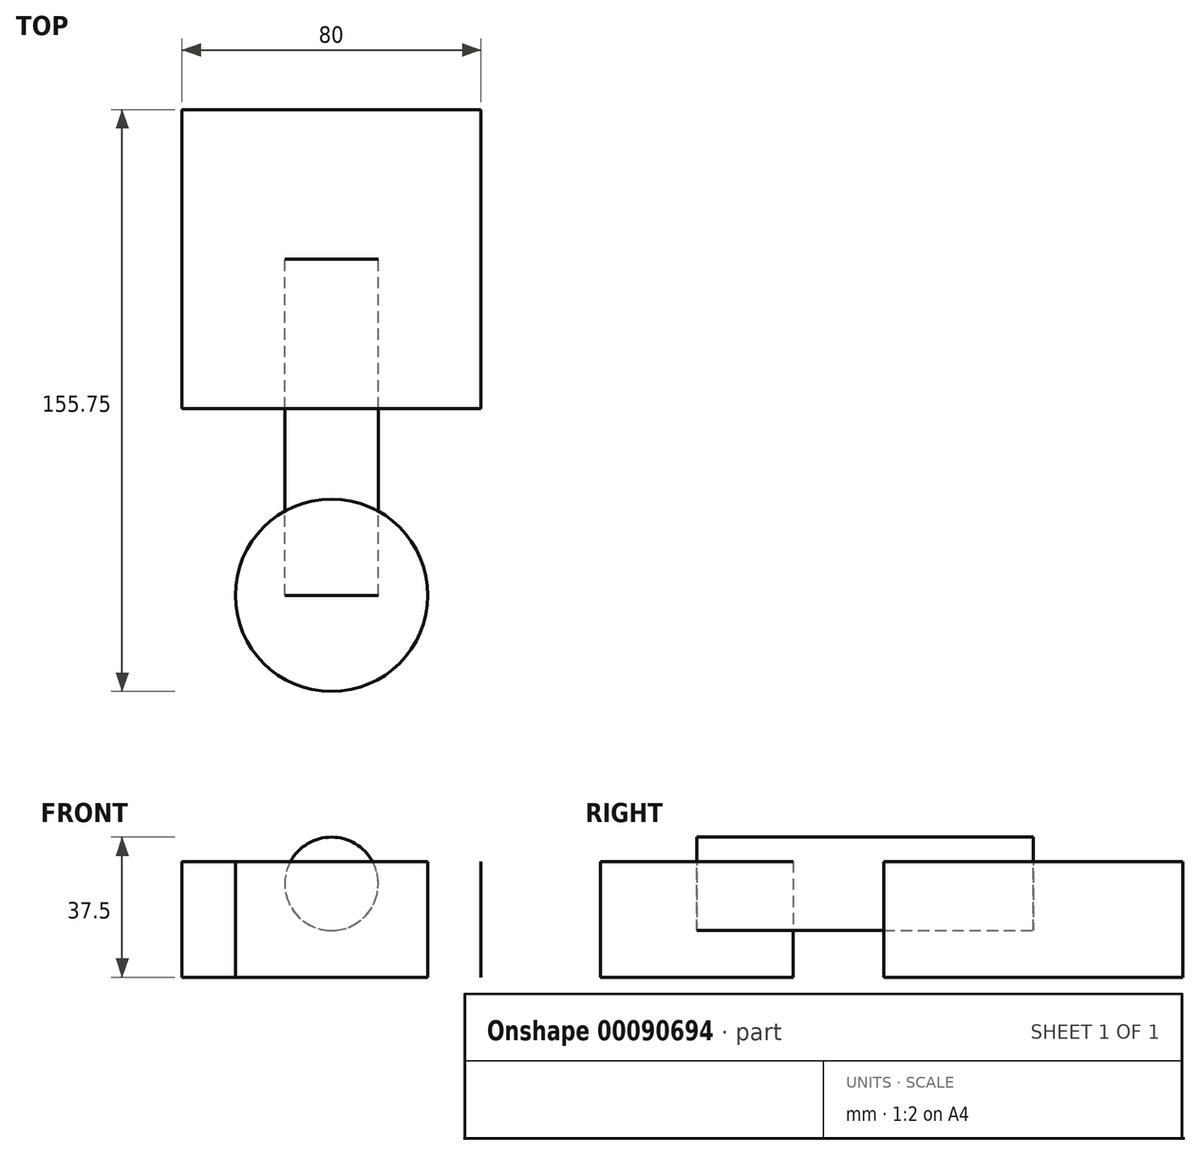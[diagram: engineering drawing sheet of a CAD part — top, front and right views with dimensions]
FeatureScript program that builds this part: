
annotation { "Feature Type Name" : "Feature", "Feature Type Description" : "" }
export const myFeature = defineFeature(function(context is Context, id is Id, definition is map)
    precondition{}
    {
        {
            var Q0;
            Q0=qCreatedBy(makeId("Top.planeOp"),FACE);
            var sketch = newSketch(context, id + "F0", { "sketchPlane" : qUnion([Q0])});
            skLineSegment(sketch, "E0.bottom", {"start": v(-60.12, 58.35) * mm, "end": v(19.88, 58.35) * mm});
            skLineSegment(sketch, "E0.top", {"start": v(-60.12, -21.65) * mm, "end": v(19.88, -21.65) * mm});
            skLineSegment(sketch, "E0.left", {"start": v(-60.12, 58.35) * mm, "end": v(-60.12, -21.65) * mm});
            skLineSegment(sketch, "E0.right", {"start": v(19.88, 58.35) * mm, "end": v(19.88, -21.65) * mm});
            skSolve(sketch);
        }
        {
            var Q0;
            Q0=makeQuery(id+"F0.imprint","IMPRINT",FACE,{"disambiguationData":[TD([[makeQuery(id+"F0.imprint","IMPRINT",EDGE,{"derivedFrom":sQuery(id+"F0.wireOp",EDGE,"E0.bottom")}),-1.0]])]});
            extrude(context, id + "F1", {"entities" : qUnion([Q0]), "depth" : 31 * mm});
        }
        {
            var Q0;
            Q0=qCreatedBy(makeId("Top.planeOp"),FACE);
            var sketch = newSketch(context, id + "F2", { "sketchPlane" : qUnion([Q0])});
            skLineSegment(sketch, "E1", {"start": v(0, 0) * mm, "end": v(19.88, -21.66) * mm});
            skSolve(sketch);
        }
        {
            var Q0;
            Q0=makeQuery(id+"F1.opExtrude","SWEPT_BODY",BODY,{"disambiguationData":[OSD([sQuery(id+"F0.wireOp",EDGE,"E0.bottom"),sQuery(id+"F0.wireOp",EDGE,"E0.top"),sQuery(id+"F0.wireOp",EDGE,"E0.left"),sQuery(id+"F0.wireOp",EDGE,"E0.right")])]});
            var Q1;
            Q1=sQuery(id+"F2.wireOp",EDGE,"E1");
            transform(context, id + "F3", {"entities" : qUnion([Q0]), "transformType" : TransformType.TRANSLATION_ENTITY, "oppositeDirectionEntity" : true, "transformLine" : qUnion([Q1]), "makeCopy" : false});
        }
        {
            var Q0;
            Q0=makeQuery(id+"F1.opExtrude","SWEPT_BODY",BODY,{"disambiguationData":[OSD([sQuery(id+"F0.wireOp",EDGE,"E0.bottom"),sQuery(id+"F0.wireOp",EDGE,"E0.top"),sQuery(id+"F0.wireOp",EDGE,"E0.left"),sQuery(id+"F0.wireOp",EDGE,"E0.right")])]});
            transform(context, id + "F4", {"entities" : qUnion([Q0]), "transformType" : TransformType.TRANSLATION_3D, "dx" : 40 * mm, "dy" : -40 * mm, "dz" : 0 * mm, "makeCopy" : false});
        }
        {
            var Q0;
            Q0=qCreatedBy(makeId("Top.planeOp"),FACE);
            var sketch = newSketch(context, id + "F5", { "sketchPlane" : qUnion([Q0])});
            skCircle(sketch, "E2", {"center": v(0, -80) * mm, "radius": 25.75 * mm});
            skSolve(sketch);
        }
        {
            var Q0;
            Q0=makeQuery(id+"F5.imprint","IMPRINT",FACE,{"disambiguationData":[TD([[makeQuery(id+"F5.imprint","IMPRINT",EDGE,{"derivedFrom":sQuery(id+"F5.wireOp",EDGE,"E2")}),1.0]])]});
            extrude(context, id + "F6", {"entities" : qUnion([Q0]), "depth" : 31 * mm});
        }
        {
            var Q0;
            Q0=makeQuery(id+"F6.opExtrude","SWEPT_BODY",BODY,{"disambiguationData":[OSD([sQuery(id+"F5.wireOp",EDGE,"E2")])]});
            transform(context, id + "F7", {"entities" : qUnion([Q0]), "transformType" : TransformType.TRANSLATION_3D, "dx" : 0 * mm, "dy" : -10 * mm, "dz" : 0 * mm, "makeCopy" : false});
        }
        {
            var Q0;
            Q0=qCreatedBy(makeId("Front.planeOp"),FACE);
            var sketch = newSketch(context, id + "F8", { "sketchPlane" : qUnion([Q0])});
            skCircle(sketch, "E3", {"center": v(0, 0) * mm, "radius": 12.5 * mm});
            skSolve(sketch);
        }
        {
            var Q0;
            Q0=makeQuery(id+"F8.imprint","IMPRINT",FACE,{"disambiguationData":[TD([[makeQuery(id+"F8.imprint","IMPRINT",EDGE,{"derivedFrom":sQuery(id+"F8.wireOp",EDGE,"E3")}),1.0]])]});
            extrude(context, id + "F9", {"entities" : qUnion([Q0]), "depth" : 90 * mm});
        }
        {
            var Q0;
            Q0=makeQuery(id+"F9.opExtrude","SWEPT_BODY",BODY,{"disambiguationData":[OSD([sQuery(id+"F8.wireOp",EDGE,"E3")])]});
            transform(context, id + "F10", {"entities" : qUnion([Q0]), "transformType" : TransformType.TRANSLATION_3D, "dx" : 0 * mm, "dy" : 0 * mm, "dz" : 25 * mm, "makeCopy" : false});
        }
    });
